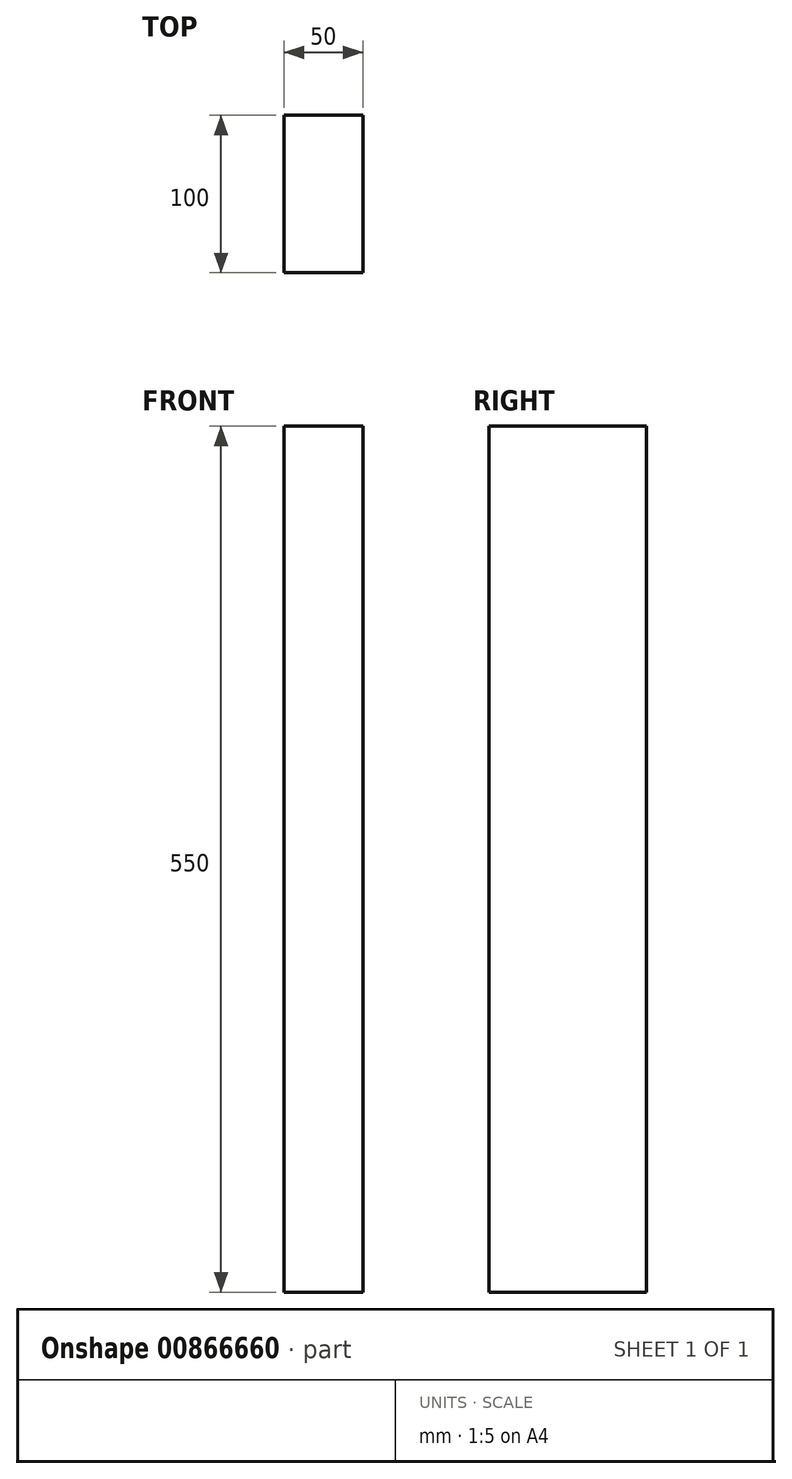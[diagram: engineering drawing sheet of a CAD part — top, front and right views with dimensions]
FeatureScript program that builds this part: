
annotation { "Feature Type Name" : "Feature", "Feature Type Description" : "" }
export const myFeature = defineFeature(function(context is Context, id is Id, definition is map)
    precondition{}
    {
        {
            var Q0;
            Q0=qCreatedBy(makeId("Top.planeOp"),FACE);
            var sketch = newSketch(context, id + "F0", { "sketchPlane" : qUnion([Q0])});
            skLineSegment(sketch, "E0.bottom", {"start": v(25, 50) * mm, "end": v(-25, 50) * mm});
            skLineSegment(sketch, "E0.top", {"start": v(25, -50) * mm, "end": v(-25, -50) * mm});
            skLineSegment(sketch, "E0.left", {"start": v(25, 50) * mm, "end": v(25, -50) * mm});
            skLineSegment(sketch, "E0.right", {"start": v(-25, 50) * mm, "end": v(-25, -50) * mm});
            skPoint(sketch, "E0.middle", {"position": v(0, 0) * mm});
            skSolve(sketch);
        }
        {
            var Q0;
            Q0=makeQuery(id+"F0.imprint","IMPRINT",FACE,{"disambiguationData":[TD([[makeQuery(id+"F0.imprint","IMPRINT",EDGE,{"derivedFrom":sQuery(id+"F0.wireOp",EDGE,"E0.bottom")}),1.0]])]});
            extrude(context, id + "F1", {"entities" : qUnion([Q0]), "depth" : 550 * mm, "offsetDistance" : 25 * mm});
        }
        {
            var Q0;
            Q0=makeQuery(id+"F1.opExtrude","SWEPT_FACE",FACE,{"disambiguationData":[OSD([sQuery(id+"F0.wireOp",EDGE,"E0.top")])]});
            var sketch = newSketch(context, id + "F2", { "sketchPlane" : qUnion([Q0])});
            skLineSegment(sketch, "E1", {"start": v(-15, 0) * mm, "end": v(-15, 550) * mm});
            skLineSegment(sketch, "E2", {"start": v(15, 550) * mm, "end": v(15, 0) * mm});
            skPoint(sketch, "E3", {"position": v(-15, 150) * mm});
            skPoint(sketch, "E4", {"position": v(15, 150) * mm});
            skPoint(sketch, "E5", {"position": v(-15, 350) * mm});
            skPoint(sketch, "E6", {"position": v(15, 350) * mm});
            skSolve(sketch);
        }
    });
